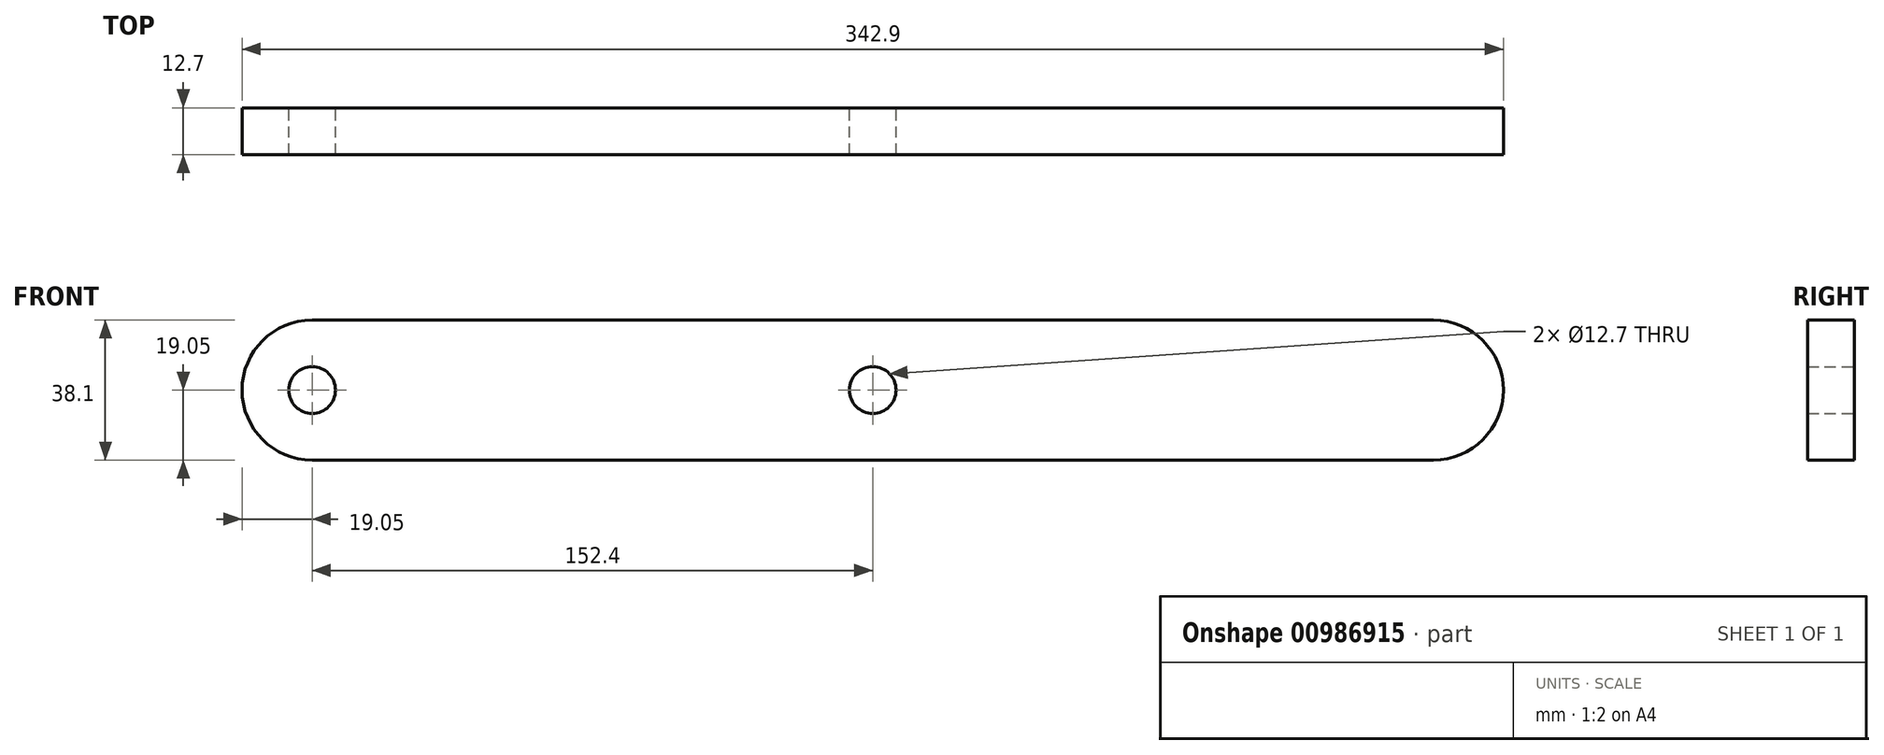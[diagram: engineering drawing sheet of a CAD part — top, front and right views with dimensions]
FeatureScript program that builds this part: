
annotation { "Feature Type Name" : "Feature", "Feature Type Description" : "" }
export const myFeature = defineFeature(function(context is Context, id is Id, definition is map)
    precondition{}
    {
        {
            var Q0;
            Q0=qCreatedBy(makeId("Front.planeOp"),FACE);
            var sketch = newSketch(context, id + "F0", { "sketchPlane" : qUnion([Q0])});
            skCircle(sketch, "E0", {"center": v(0, 0) * mm, "radius": 6.35 * mm});
            skCircle(sketch, "E1", {"center": v(304.8, 0) * mm, "radius": 6.35 * mm, "construction": true});
            skArc(sketch, "E2", {"start": v(0, 19.05) * mm, "mid": v(-19.05, 0) * mm, "end": v(0, -19.05) * mm});
            skArc(sketch, "E3", {"start": v(304.8, -19.05) * mm, "mid": v(323.85, 0) * mm, "end": v(304.8, 19.05) * mm});
            skLineSegment(sketch, "E4", {"start": v(0, 19.05) * mm, "end": v(304.8, 19.05) * mm});
            skLineSegment(sketch, "E5", {"start": v(0, -19.05) * mm, "end": v(304.8, -19.05) * mm});
            skCircle(sketch, "E6", {"center": v(152.4, 0) * mm, "radius": 6.35 * mm});
            skSolve(sketch);
        }
        {
            var Q0;
            Q0=qSketchRegion(id+"F0",true);
            extrude(context, id + "F1", {"entities" : qUnion([Q0]), "endBound" : BoundingType.SYMMETRIC, "depth" : 12.7 * mm, "offsetDistance" : 25.4 * mm});
        }
    });
